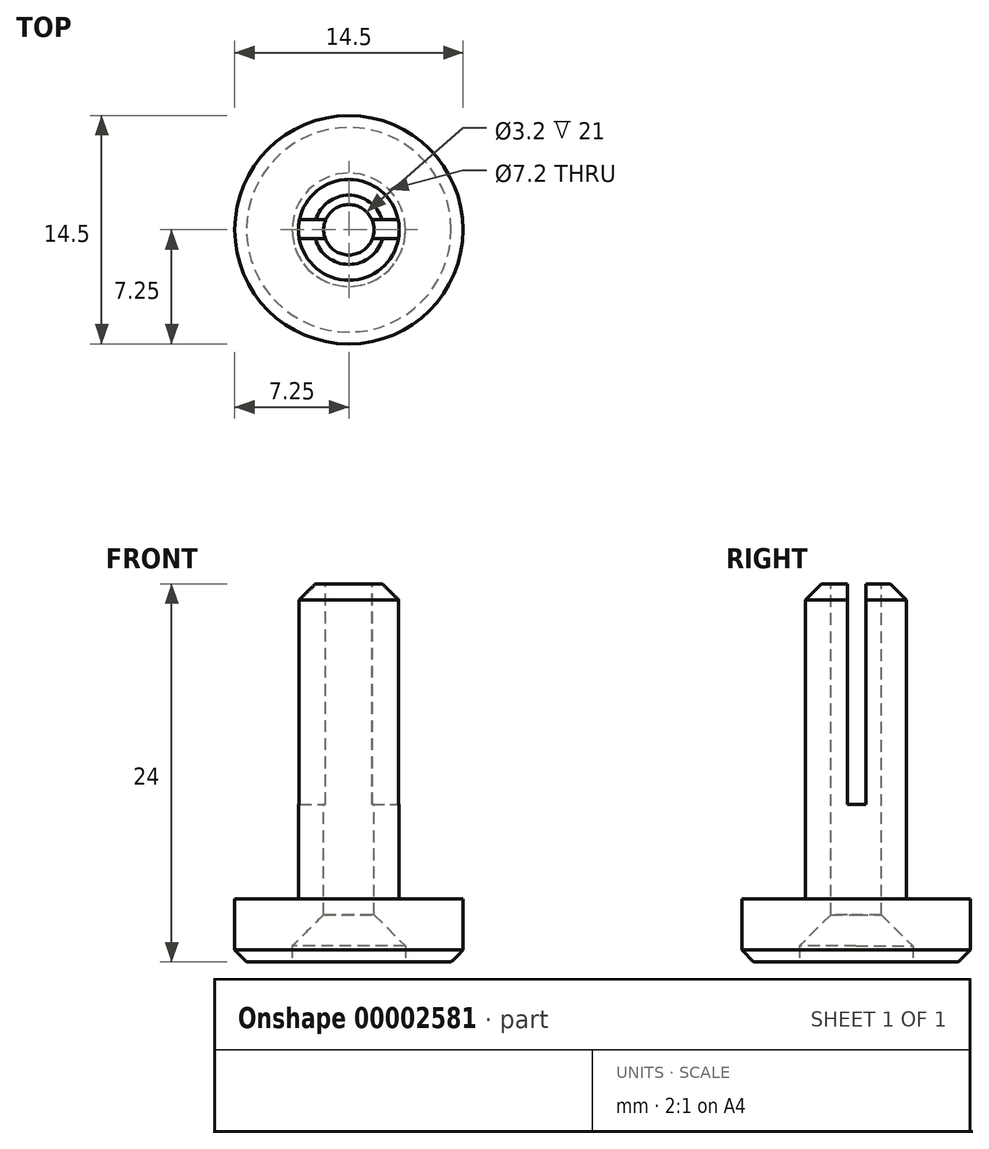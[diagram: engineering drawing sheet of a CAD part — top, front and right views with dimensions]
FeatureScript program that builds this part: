
annotation { "Feature Type Name" : "Feature", "Feature Type Description" : "" }
export const myFeature = defineFeature(function(context is Context, id is Id, definition is map)
    precondition{}
    {
        {
            var Q0;
            Q0=qCreatedBy(makeId("Top.planeOp"),FACE);
            var sketch = newSketch(context, id + "F0", { "sketchPlane" : qUnion([Q0])});
            skCircle(sketch, "E0", {"center": v(0, 0) * mm, "radius": 7.25 * mm});
            skSolve(sketch);
        }
        {
            var Q0;
            Q0=makeQuery(id+"F0.imprint","IMPRINT",FACE,{"disambiguationData":[TD([[makeQuery(id+"F0.imprint","IMPRINT",EDGE,{"derivedFrom":sQuery(id+"F0.wireOp",EDGE,"E0")}),1.0]])]});
            extrude(context, id + "F1", {"entities" : qUnion([Q0]), "depth" : 4 * mm});
        }
        {
            var Q0;
            Q0=makeQuery(id+"F0.imprint","IMPRINT",FACE,{"disambiguationData":[TD([[makeQuery(id+"F0.imprint","IMPRINT",EDGE,{"derivedFrom":sQuery(id+"F0.wireOp",EDGE,"E0")}),1.0]])]});
            var sketch = newSketch(context, id + "F2", { "sketchPlane" : qUnion([Q0])});
            skCircle(sketch, "E1", {"center": v(0, 0) * mm, "radius": 3.6 * mm});
            skSolve(sketch);
        }
        {
            var Q0;
            Q0=makeQuery(id+"F2.imprint","IMPRINT",FACE,{"disambiguationData":[TD([[makeQuery(id+"F2.imprint","IMPRINT",EDGE,{"derivedFrom":sQuery(id+"F2.wireOp",EDGE,"E1")}),1.0]])]});
            extrude(context, id + "F3", {"entities" : qUnion([Q0]), "operationType" : NewBodyOperationType.REMOVE, "depth" : 3 * mm});
        }
        {
            var Q0;
            Q0=makeQuery(id+"F1.opExtrude","CAP_FACE",FACE,{"disambiguationData":[OSD([sQuery(id+"F0.wireOp",EDGE,"E0")])],"isStart":false});
            var sketch = newSketch(context, id + "F4", { "sketchPlane" : qUnion([Q0])});
            skCircle(sketch, "E2", {"center": v(0, 0) * mm, "radius": 3.2 * mm});
            skSolve(sketch);
        }
        {
            var Q0;
            Q0=makeQuery(id+"F4.imprint","IMPRINT",FACE,{"disambiguationData":[TD([[makeQuery(id+"F4.imprint","IMPRINT",EDGE,{"derivedFrom":sQuery(id+"F4.wireOp",EDGE,"E2")}),1.0]])]});
            extrude(context, id + "F5", {"entities" : qUnion([Q0]), "operationType" : NewBodyOperationType.ADD, "depth" : 20 * mm});
        }
        {
            var Q0;
            Q0=makeQuery(id+"F1.opExtrude","CAP_EDGE",EDGE,{"disambiguationData":[OSD([sQuery(id+"F0.wireOp",EDGE,"E0")])],"isStart":true});
            chamfer(context, id + "F6", {"entities" : qUnion([Q0]), "width" : .75 * mm, "tangentPropagation" : true});
        }
        {
            var Q0;
            Q0=makeQuery(id+"F3.boolean.opBoolean","COPY",EDGE,{"derivedFrom":makeQuery(id+"F3.opExtrude","CAP_EDGE",EDGE,{"disambiguationData":[OSD([sQuery(id+"F2.wireOp",EDGE,"E1")])],"isStart":false})});
            chamfer(context, id + "F7", {"entities" : qUnion([Q0]), "width" : 2 * mm, "tangentPropagation" : true});
        }
        {
            var Q0;
            Q0=makeQuery(id+"F5.opExtrude","CAP_FACE",FACE,{"disambiguationData":[OSD([sQuery(id+"F4.wireOp",EDGE,"E2")])],"isStart":false});
            var sketch = newSketch(context, id + "F8", { "sketchPlane" : qUnion([Q0])});
            skCircle(sketch, "E3", {"center": v(0, 0) * mm, "radius": 1.6 * mm});
            skSolve(sketch);
        }
        {
            var Q0;
            Q0 = qSketchRegion(id + "F8", true);
            extrude(context, id + "F9", {"entities" : qUnion([Q0]), "operationType" : NewBodyOperationType.REMOVE, "endBound" : BoundingType.THROUGH_ALL, "oppositeDirection" : true, "depth" : 25 * mm});
        }
        {
            var Q0;
            Q0=makeQuery(id+"F5.opExtrude","CAP_FACE",FACE,{"disambiguationData":[OSD([sQuery(id+"F4.wireOp",EDGE,"E2")])],"isStart":false});
            var sketch = newSketch(context, id + "F10", { "sketchPlane" : qUnion([Q0])});
            skLineSegment(sketch, "E4.bottom", {"start": v(-5.54, 0.64) * mm, "end": v(5.3, 0.64) * mm});
            skLineSegment(sketch, "E4.top", {"start": v(-5.54, -0.56) * mm, "end": v(5.3, -0.56) * mm});
            skLineSegment(sketch, "E4.left", {"start": v(-5.54, 0.64) * mm, "end": v(-5.54, -0.56) * mm});
            skLineSegment(sketch, "E4.right", {"start": v(5.3, 0.64) * mm, "end": v(5.3, -0.56) * mm});
            skSolve(sketch);
        }
        {
            var Q0;
            Q0 = qSketchRegion(id + "F10", true);
            extrude(context, id + "F11", {"entities" : qUnion([Q0]), "operationType" : NewBodyOperationType.REMOVE, "oppositeDirection" : true, "depth" : 14 * mm});
        }
        {
            var Q0;
            {var subQ0=sQuery(id+"F4.wireOp",EDGE,"E2");Q0=makeQuery(id+"F11.boolean.opBoolean","SPLIT",EDGE,{"disambiguationData":[TD([makeQuery(id+"F11.opExtrude","SWEPT_FACE",FACE,{"disambiguationData":[OSD([sQuery(id+"F10.wireOp",EDGE,"E4.top")])]})])],"derivedFrom":makeQuery(id+"F5.opExtrude","CAP_EDGE",EDGE,{"disambiguationData":[OSD([subQ0])],"isStart":false})});}
            var Q1;
            {var subQ0=sQuery(id+"F4.wireOp",EDGE,"E2");Q1=makeQuery(id+"F11.boolean.opBoolean","SPLIT",EDGE,{"disambiguationData":[TD([makeQuery(id+"F11.opExtrude","SWEPT_FACE",FACE,{"disambiguationData":[OSD([sQuery(id+"F10.wireOp",EDGE,"E4.bottom")])]})])],"derivedFrom":makeQuery(id+"F5.opExtrude","CAP_EDGE",EDGE,{"disambiguationData":[OSD([subQ0])],"isStart":false})});}
            chamfer(context, id + "F12", {"entities" : qUnion([Q0, Q1]), "width" : 1 * mm, "tangentPropagation" : true});
        }
    });
